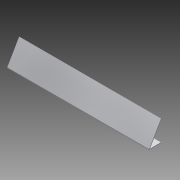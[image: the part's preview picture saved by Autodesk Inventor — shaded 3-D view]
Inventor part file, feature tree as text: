
AUTODESK INVENTOR PART (.ipt)
format: ipt  version: 2015 SP1 (Build 190203100, 203)  size: 126,464 bytes
history: native  units: in
note: dims shown in document units (in); Inventor stores cm internally (conversion verified against a paired STEP export)
features: sketch x3, extrude x2, hole x1
ambient origin geometry x8: Origin, YZ Plane, XZ Plane, XY Plane, X Axis, Y Axis, Z Axis, Center Point
bodies: Solid1 (feature_tree)
feature tree (6):
  extrude  "Extrusion1"  Depth=2.0in
  hole  "Hole1"  [1 undecoded]
  extrude  "Extrusion4"  Depth=12.0in TaperAngle=0.0deg
  sketch  "Sketch1"  dims[d0=0.0625in d1=2.0in]
  sketch  "Sketch2"  dims[d2=2.0in d3=30.0deg]
  sketch  "Sketch5"  dims[d4=0.0625in d5=12.0in d6=0.0in d7=1.125in d8=1.125in d9=5.0in d10=7.0in d11=0.25in d12=0.75in d13=0.375in d14=0.25in d15=0.5635in d16=0.25in d17=0.8108in d28=4.0in d29=1.0in d30=4.0in d31=1.0in d32=1.0in d33=1.0in d34=0.25in d35=0.0in]
note: 1 required parameter value undecoded (feature->parameter linkage not recoverable at this tier; creation-order binding heuristic only, values carry confidence <= 0.55)
